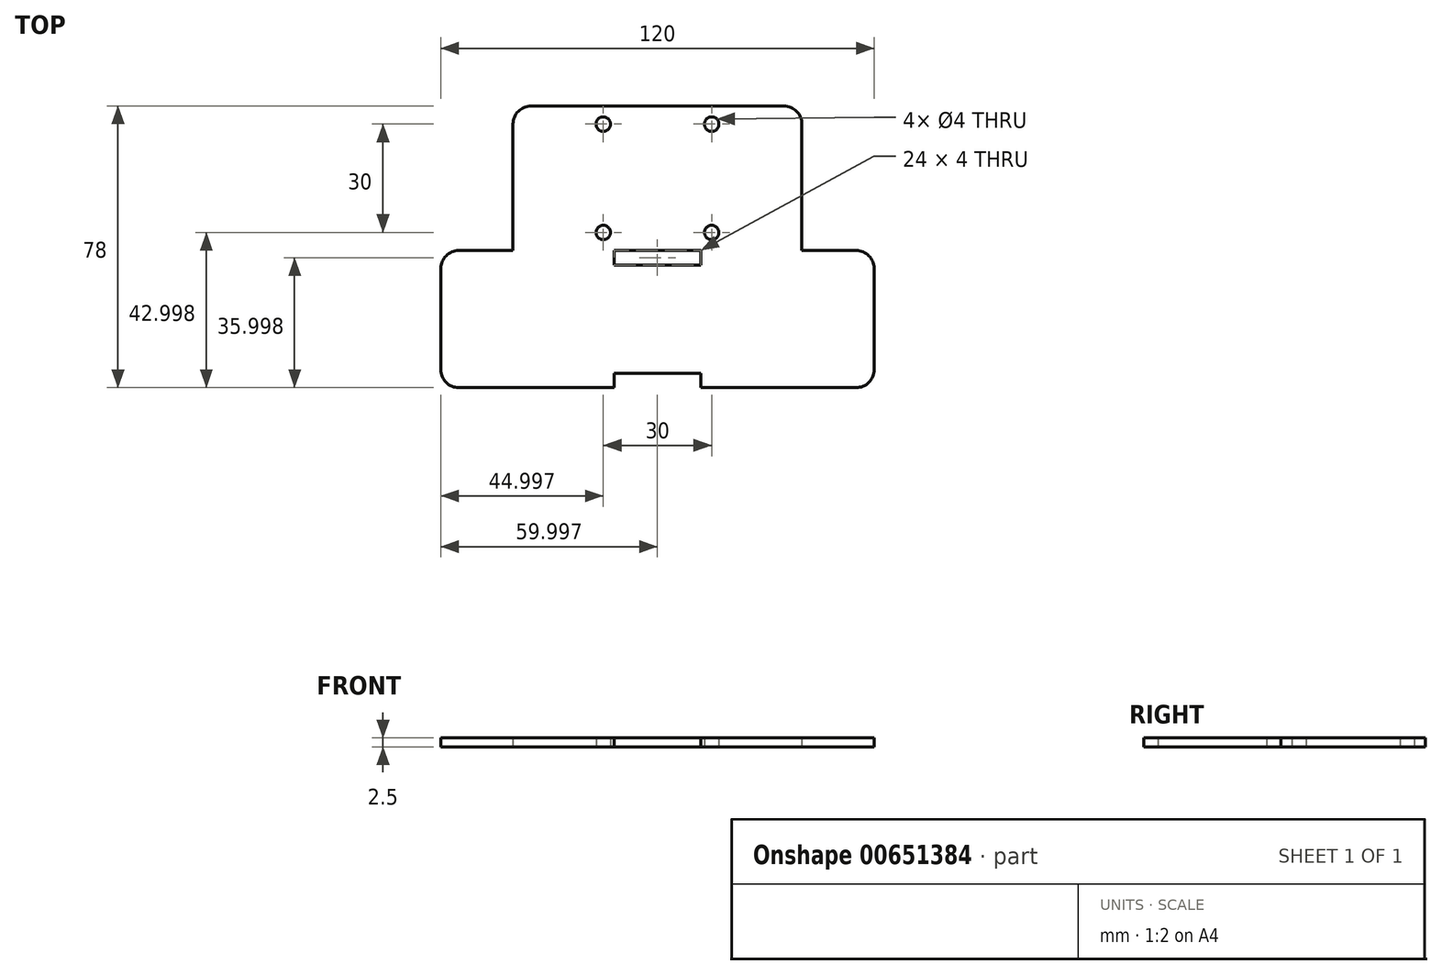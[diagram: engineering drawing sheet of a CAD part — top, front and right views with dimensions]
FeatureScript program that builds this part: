
annotation { "Feature Type Name" : "Feature", "Feature Type Description" : "" }
export const myFeature = defineFeature(function(context is Context, id is Id, definition is map)
    precondition{}
    {
        {
            var Q0;
            Q0=qCreatedBy(makeId("Top.planeOp"),FACE);
            var sketch = newSketch(context, id + "F0", { "sketchPlane" : qUnion([Q0])});
            skLineSegment(sketch, "E0.bottom", {"start": v(-51.88, 6.2) * mm, "end": v(-16.88, 6.2) * mm});
            skLineSegment(sketch, "E0.top", {"start": v(-51.88, -31.8) * mm, "end": v(58.12, -31.8) * mm});
            skLineSegment(sketch, "E0.left", {"start": v(-56.88, 1.2) * mm, "end": v(-56.88, -26.8) * mm});
            skLineSegment(sketch, "E0.right", {"start": v(63.12, 1.2) * mm, "end": v(63.12, -26.8) * mm});
            skLineSegment(sketch, "E1", {"start": v(-16.88, 6.2) * mm, "end": v(-16.88, 41.2) * mm});
            skLineSegment(sketch, "E2", {"start": v(-11.88, 46.2) * mm, "end": v(18.12, 46.2) * mm});
            skLineSegment(sketch, "E3", {"start": v(23.12, 41.2) * mm, "end": v(23.12, 6.2) * mm});
            skCircle(sketch, "E4", {"center": v(-11.88, 41.2) * mm, "radius": 2 * mm});
            skCircle(sketch, "E5", {"center": v(18.12, 41.2) * mm, "radius": 2 * mm});
            skCircle(sketch, "E6", {"center": v(-11.88, 11.2) * mm, "radius": 2 * mm});
            skCircle(sketch, "E7", {"center": v(18.12, 11.2) * mm, "radius": 2 * mm});
            skLineSegment(sketch, "E8", {"start": v(-8.88, -31.8) * mm, "end": v(-8.88, -27.8) * mm});
            skLineSegment(sketch, "E9", {"start": v(-8.88, -27.8) * mm, "end": v(15.12, -27.8) * mm});
            skLineSegment(sketch, "E10", {"start": v(15.12, -27.8) * mm, "end": v(15.12, -31.8) * mm});
            skLineSegment(sketch, "E11.bottom", {"start": v(-8.88, 6.2) * mm, "end": v(15.12, 6.2) * mm});
            skLineSegment(sketch, "E11.top", {"start": v(-8.88, 2.2) * mm, "end": v(15.12, 2.2) * mm});
            skLineSegment(sketch, "E11.left", {"start": v(-8.88, 6.2) * mm, "end": v(-8.88, 2.2) * mm});
            skLineSegment(sketch, "E11.right", {"start": v(15.12, 6.2) * mm, "end": v(15.12, 2.2) * mm});
            skPoint(sketch, "E12", {"position": v(3.12, -31.8) * mm});
            skPoint(sketch, "E13", {"position": v(3.12, -27.8) * mm});
            skPoint(sketch, "E14", {"position": v(3.12, 46.2) * mm});
            skLineSegment(sketch, "E15", {"start": v(-11.88, 41.2) * mm, "end": v(18.12, 41.2) * mm, "construction": true});
            skPoint(sketch, "E16", {"position": v(3.12, 41.2) * mm});
            skPoint(sketch, "E17.visualSharp", {"position": v(-56.88, 6.2) * mm});
            skArc(sketch, "E17.filletArc", {"start": v(-51.88, 6.2) * mm, "mid": v(-55.42, 4.73) * mm, "end": v(-56.88, 1.2) * mm});
            skPoint(sketch, "E18.visualSharp", {"position": v(-56.88, -31.8) * mm});
            skArc(sketch, "E18.filletArc", {"start": v(-56.88, -26.8) * mm, "mid": v(-55.42, -30.34) * mm, "end": v(-51.88, -31.8) * mm});
            skPoint(sketch, "E19.visualSharp", {"position": v(63.12, -31.8) * mm});
            skArc(sketch, "E19.filletArc", {"start": v(58.12, -31.8) * mm, "mid": v(61.65, -30.34) * mm, "end": v(63.12, -26.8) * mm});
            skPoint(sketch, "E20.visualSharp", {"position": v(63.12, 6.2) * mm});
            skArc(sketch, "E20.filletArc", {"start": v(63.12, 1.2) * mm, "mid": v(61.65, 4.73) * mm, "end": v(58.12, 6.2) * mm});
            skPoint(sketch, "E21.visualSharp", {"position": v(23.12, 46.2) * mm});
            skArc(sketch, "E21.filletArc", {"start": v(23.12, 41.2) * mm, "mid": v(21.65, 44.73) * mm, "end": v(18.12, 46.2) * mm});
            skPoint(sketch, "E22.visualSharp", {"position": v(-16.88, 46.2) * mm});
            skArc(sketch, "E22.filletArc", {"start": v(-11.88, 46.2) * mm, "mid": v(-15.42, 44.73) * mm, "end": v(-16.88, 41.2) * mm});
            skLineSegment(sketch, "E23.trimOffspring", {"start": v(23.12, 6.2) * mm, "end": v(58.12, 6.2) * mm});
            skLineSegment(sketch, "E24", {"start": v(-16.88, 46.2) * mm, "end": v(-31.88, 46.2) * mm});
            skLineSegment(sketch, "E25", {"start": v(-36.88, 41.2) * mm, "end": v(-36.88, 6.2) * mm});
            skLineSegment(sketch, "E26", {"start": v(3.12, 46.2) * mm, "end": v(3.12, -27.8) * mm, "construction": true});
            skLineSegment(sketch, "E27", {"start": v(-16.88, 46.2) * mm, "end": v(-11.88, 46.2) * mm});
            skLineSegment(sketch, "E28.MirrorCS", {"start": v(43.12, 41.2) * mm, "end": v(43.12, 6.2) * mm});
            skLineSegment(sketch, "E29.MirrorCS", {"start": v(23.12, 46.2) * mm, "end": v(38.12, 46.2) * mm});
            skLineSegment(sketch, "E30.MirrorCS", {"start": v(23.12, 46.2) * mm, "end": v(18.12, 46.2) * mm});
            skPoint(sketch, "E31.visualSharp", {"position": v(-36.88, 46.2) * mm});
            skArc(sketch, "E31.filletArc", {"start": v(-31.88, 46.2) * mm, "mid": v(-35.42, 44.73) * mm, "end": v(-36.88, 41.2) * mm});
            skPoint(sketch, "E32.visualSharp", {"position": v(43.12, 46.2) * mm});
            skArc(sketch, "E32.filletArc", {"start": v(43.12, 41.2) * mm, "mid": v(41.65, 44.73) * mm, "end": v(38.12, 46.2) * mm});
            skSolve(sketch);
        }
        {
            var Q0;
            Q0=makeQuery(id+"F0.imprint","IMPRINT",FACE,{"disambiguationData":[TD([[makeQuery(id+"F0.imprint","IMPRINT",EDGE,{"derivedFrom":sQuery(id+"F0.wireOp",EDGE,"E0.bottom")}),-1.0]])]});
            var Q1;
            {var subQ0=sQuery(id+"F0.wireOp",EDGE,"E1");Q1=makeQuery(id+"F0.imprint","IMPRINT",FACE,{"disambiguationData":[TD([[makeQuery(id+"F0.imprint","IMPRINT",EDGE,{"derivedFrom":subQ0}),1.0]])]});}
            var Q2;
            {var subQ2=sQuery(id+"F0.wireOp",EDGE,"E3");Q2=makeQuery(id+"F0.imprint","IMPRINT",FACE,{"disambiguationData":[TD([[makeQuery(id+"F0.imprint","IMPRINT",EDGE,{"derivedFrom":subQ2}),1.0]])]});}
            extrude(context, id + "F1", {"entities" : qUnion([Q0, Q1, Q2]), "depth" : 2.5 * mm, "offsetDistance" : 25 * mm});
        }
    });
